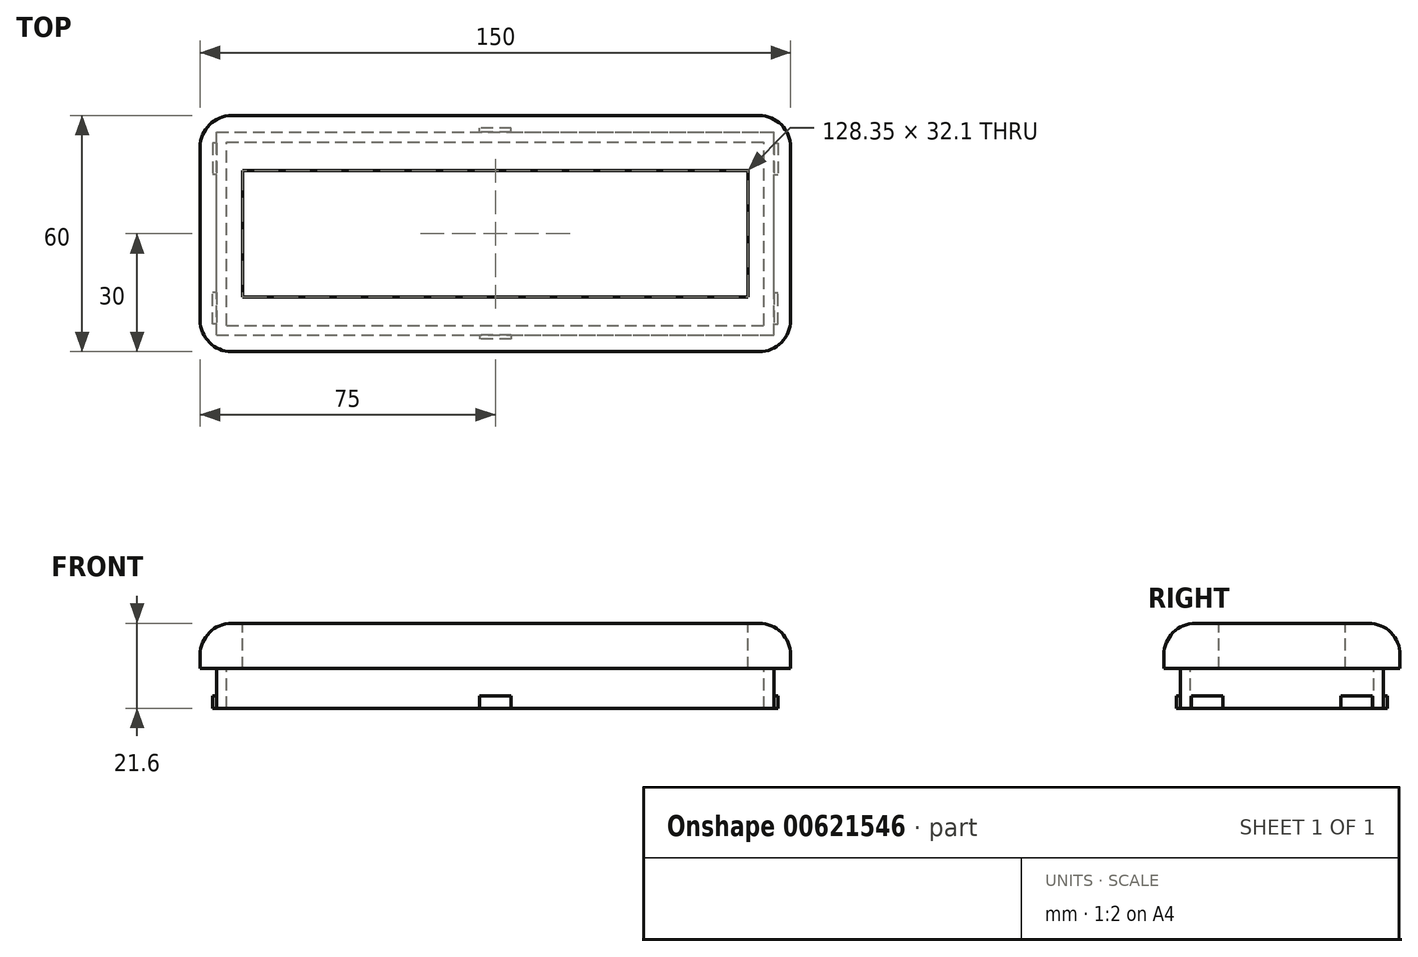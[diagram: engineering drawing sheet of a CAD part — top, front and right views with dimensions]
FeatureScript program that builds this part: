
annotation { "Feature Type Name" : "Feature", "Feature Type Description" : "" }
export const myFeature = defineFeature(function(context is Context, id is Id, definition is map)
    precondition{}
    {
        {
            var Q0;
            Q0=qCreatedBy(makeId("Top.planeOp"),FACE);
            var sketch = newSketch(context, id + "F0", { "sketchPlane" : qUnion([Q0])});
            skLineSegment(sketch, "E0.bottom", {"start": v(75, -30) * mm, "end": v(-75, -30) * mm});
            skLineSegment(sketch, "E0.top", {"start": v(75, 30) * mm, "end": v(-75, 30) * mm});
            skLineSegment(sketch, "E0.left", {"start": v(75, -30) * mm, "end": v(75, 30) * mm});
            skLineSegment(sketch, "E0.right", {"start": v(-75, -30) * mm, "end": v(-75, 30) * mm});
            skPoint(sketch, "E0.middle", {"position": v(0, 0) * mm});
            skSolve(sketch);
        }
        {
            var Q0;
            Q0 = qSketchRegion(id + "F0", true);
            extrude(context, id + "F1", {"entities" : qUnion([Q0]), "depth" : 11.5 * mm, "offsetDistance" : 25 * mm});
        }
        {
            var Q0;
            Q0=makeQuery(id+"F1.opExtrude","CAP_FACE",FACE,{"disambiguationData":[OSD([sQuery(id+"F0.wireOp",EDGE,"E0.bottom"),sQuery(id+"F0.wireOp",EDGE,"E0.top"),sQuery(id+"F0.wireOp",EDGE,"E0.left"),sQuery(id+"F0.wireOp",EDGE,"E0.right")])],"isStart":false});
            var sketch = newSketch(context, id + "F2", { "sketchPlane" : qUnion([Q0])});
            skLineSegment(sketch, "E1.bottom", {"start": v(64.17, 16.05) * mm, "end": v(-64.17, 16.05) * mm});
            skLineSegment(sketch, "E1.top", {"start": v(64.17, -16.05) * mm, "end": v(-64.17, -16.05) * mm});
            skLineSegment(sketch, "E1.left", {"start": v(64.17, 16.05) * mm, "end": v(64.17, -16.05) * mm});
            skLineSegment(sketch, "E1.right", {"start": v(-64.17, 16.05) * mm, "end": v(-64.17, -16.05) * mm});
            skPoint(sketch, "E1.middle", {"position": v(0, 0) * mm});
            skSolve(sketch);
        }
        {
            var Q0;
            Q0=makeQuery(id+"F2.imprint","IMPRINT",FACE,{"disambiguationData":[TD([[makeQuery(id+"F2.imprint","IMPRINT",EDGE,{"derivedFrom":sQuery(id+"F2.wireOp",EDGE,"E1.bottom")}),1.0]])]});
            extrude(context, id + "F3", {"entities" : qUnion([Q0]), "operationType" : NewBodyOperationType.REMOVE, "endBound" : BoundingType.UP_TO_NEXT, "oppositeDirection" : true, "depth" : 25 * mm, "offsetDistance" : 25 * mm});
        }
        {
            var Q0;
            Q0=makeQuery(id+"F1.opExtrude","SWEPT_EDGE",EDGE,{"disambiguationData":[OSD([sQuery(id+"F0.wireOp",EDGE,"E0.top"),sQuery(id+"F0.wireOp",EDGE,"E0.right")])]});
            var Q1;
            Q1=makeQuery(id+"F1.opExtrude","SWEPT_EDGE",EDGE,{"disambiguationData":[OSD([sQuery(id+"F0.wireOp",EDGE,"E0.top"),sQuery(id+"F0.wireOp",EDGE,"E0.left")])]});
            var Q2;
            Q2=makeQuery(id+"F1.opExtrude","SWEPT_EDGE",EDGE,{"disambiguationData":[OSD([sQuery(id+"F0.wireOp",EDGE,"E0.bottom"),sQuery(id+"F0.wireOp",EDGE,"E0.left")])]});
            var Q3;
            Q3=makeQuery(id+"F1.opExtrude","SWEPT_EDGE",EDGE,{"disambiguationData":[OSD([sQuery(id+"F0.wireOp",EDGE,"E0.bottom"),sQuery(id+"F0.wireOp",EDGE,"E0.right")])]});
            fillet(context, id + "F4", {"entities" : qUnion([Q0, Q1, Q2, Q3]), "radius" : 8 * mm, "tangentPropagation" : true, "allowEdgeOverflow" : false});
        }
        {
            var Q0;
            Q0=makeQuery(id+"F1.opExtrude","CAP_FACE",FACE,{"disambiguationData":[OSD([sQuery(id+"F0.wireOp",EDGE,"E0.bottom"),sQuery(id+"F0.wireOp",EDGE,"E0.top"),sQuery(id+"F0.wireOp",EDGE,"E0.left"),sQuery(id+"F0.wireOp",EDGE,"E0.right")])],"isStart":true});
            var sketch = newSketch(context, id + "F5", { "sketchPlane" : qUnion([Q0])});
            skLineSegment(sketch, "E2.bottom", {"start": v(-70.8, 25.8) * mm, "end": v(70.8, 25.8) * mm});
            skLineSegment(sketch, "E2.top", {"start": v(-70.8, -25.8) * mm, "end": v(70.8, -25.8) * mm});
            skLineSegment(sketch, "E2.left", {"start": v(-70.8, 25.8) * mm, "end": v(-70.8, -25.8) * mm});
            skLineSegment(sketch, "E2.right", {"start": v(70.8, 25.8) * mm, "end": v(70.8, -25.8) * mm});
            skLineSegment(sketch, "E3.0", {"start": v(-68.3, 23.3) * mm, "end": v(68.3, 23.3) * mm});
            skLineSegment(sketch, "E3.1", {"start": v(-68.3, 23.3) * mm, "end": v(-68.3, -23.3) * mm});
            skLineSegment(sketch, "E3.2", {"start": v(-68.3, -23.3) * mm, "end": v(68.3, -23.3) * mm});
            skLineSegment(sketch, "E3.3", {"start": v(68.3, 23.3) * mm, "end": v(68.3, -23.3) * mm});
            skSolve(sketch);
        }
        {
            var Q0;
            Q0=makeQuery(id+"F5.imprint","IMPRINT",FACE,{"disambiguationData":[TD([[makeQuery(id+"F5.imprint","IMPRINT",EDGE,{"derivedFrom":sQuery(id+"F5.wireOp",EDGE,"E2.bottom")}),-1.0]])]});
            extrude(context, id + "F6", {"entities" : qUnion([Q0]), "operationType" : NewBodyOperationType.ADD, "depth" : 10.1 * mm, "offsetDistance" : 25 * mm});
        }
        {
            var Q0;
            Q0=makeQuery(id+"F1.opExtrude","CAP_EDGE",EDGE,{"disambiguationData":[OSD([sQuery(id+"F0.wireOp",EDGE,"E0.top")])],"isStart":false});
            fillet(context, id + "F7", {"entities" : qUnion([Q0]), "radius" : 8 * mm, "tangentPropagation" : true, "allowEdgeOverflow" : false});
        }
        {
            var Q0;
            Q0=makeQuery(id+"F6.opExtrude","CAP_FACE",FACE,{"disambiguationData":[OSD([sQuery(id+"F5.wireOp",EDGE,"E2.bottom"),sQuery(id+"F5.wireOp",EDGE,"E2.top"),sQuery(id+"F5.wireOp",EDGE,"E2.left"),sQuery(id+"F5.wireOp",EDGE,"E2.right"),sQuery(id+"F5.wireOp",EDGE,"E3.0"),sQuery(id+"F5.wireOp",EDGE,"E3.1"),sQuery(id+"F5.wireOp",EDGE,"E3.2"),sQuery(id+"F5.wireOp",EDGE,"E3.3")])],"isStart":false});
            var sketch = newSketch(context, id + "F8", { "sketchPlane" : qUnion([Q0])});
            skLineSegment(sketch, "E4.bottom", {"start": v(-70.8, 22.98) * mm, "end": v(-71.8, 22.98) * mm});
            skLineSegment(sketch, "E4.top", {"start": v(-70.8, 14.98) * mm, "end": v(-71.8, 14.98) * mm});
            skLineSegment(sketch, "E4.left", {"start": v(-70.8, 22.98) * mm, "end": v(-70.8, 14.98) * mm});
            skLineSegment(sketch, "E4.right", {"start": v(-71.8, 22.98) * mm, "end": v(-71.8, 14.98) * mm});
            skLineSegment(sketch, "E5.MirrorCS", {"start": v(70.8, 22.98) * mm, "end": v(71.8, 22.98) * mm});
            skLineSegment(sketch, "E6.MirrorCS", {"start": v(70.8, 14.98) * mm, "end": v(71.8, 14.98) * mm});
            skLineSegment(sketch, "E7.MirrorCS", {"start": v(70.8, 22.98) * mm, "end": v(70.8, 14.98) * mm});
            skLineSegment(sketch, "E8.MirrorCS", {"start": v(71.8, 22.98) * mm, "end": v(71.8, 14.98) * mm});
            skLineSegment(sketch, "E9.MirrorCS", {"start": v(-71.8, -22.98) * mm, "end": v(-71.8, -14.98) * mm});
            skLineSegment(sketch, "E10.MirrorCS", {"start": v(-70.8, -22.98) * mm, "end": v(-70.8, -14.98) * mm});
            skLineSegment(sketch, "E11.MirrorCS", {"start": v(-70.8, -14.98) * mm, "end": v(-71.8, -14.98) * mm});
            skLineSegment(sketch, "E12.MirrorCS", {"start": v(-70.8, -22.98) * mm, "end": v(-71.8, -22.98) * mm});
            skLineSegment(sketch, "E13.MirrorCS", {"start": v(71.8, -22.98) * mm, "end": v(71.8, -14.98) * mm});
            skLineSegment(sketch, "E14.MirrorCS", {"start": v(70.8, -14.98) * mm, "end": v(71.8, -14.98) * mm});
            skLineSegment(sketch, "E15.MirrorCS", {"start": v(70.8, -22.98) * mm, "end": v(70.8, -14.98) * mm});
            skLineSegment(sketch, "E16.MirrorCS", {"start": v(70.8, -22.98) * mm, "end": v(71.8, -22.98) * mm});
            skLineSegment(sketch, "E17.bottom", {"start": v(4, 25.8) * mm, "end": v(0, 25.8) * mm});
            skLineSegment(sketch, "E17.top", {"start": v(4, 26.8) * mm, "end": v(0, 26.8) * mm});
            skLineSegment(sketch, "E17.left", {"start": v(4, 25.8) * mm, "end": v(4, 26.8) * mm});
            skLineSegment(sketch, "E17.right", {"start": v(0, 25.8) * mm, "end": v(0, 26.8) * mm});
            skLineSegment(sketch, "E18.MirrorCS", {"start": v(-4, 25.8) * mm, "end": v(-4, 26.8) * mm});
            skLineSegment(sketch, "E19.MirrorCS", {"start": v(-4, 26.8) * mm, "end": v(0, 26.8) * mm});
            skLineSegment(sketch, "E20.MirrorCS", {"start": v(-4, 25.8) * mm, "end": v(0, 25.8) * mm});
            skLineSegment(sketch, "E21.MirrorCS", {"start": v(0, -25.8) * mm, "end": v(0, -26.8) * mm});
            skLineSegment(sketch, "E22.MirrorCS", {"start": v(4, -25.8) * mm, "end": v(0, -25.8) * mm});
            skLineSegment(sketch, "E23.MirrorCS", {"start": v(-4, -26.8) * mm, "end": v(0, -26.8) * mm});
            skLineSegment(sketch, "E24.MirrorCS", {"start": v(-4, -25.8) * mm, "end": v(-4, -26.8) * mm});
            skLineSegment(sketch, "E25.MirrorCS", {"start": v(-4, -25.8) * mm, "end": v(0, -25.8) * mm});
            skLineSegment(sketch, "E26.MirrorCS", {"start": v(4, -26.8) * mm, "end": v(0, -26.8) * mm});
            skLineSegment(sketch, "E27.MirrorCS", {"start": v(4, -25.8) * mm, "end": v(4, -26.8) * mm});
            skSolve(sketch);
        }
        {
            var Q0;
            {var subQ0=sQuery(id+"F0.wireOp",EDGE,"E0.right");var subQ1=sQuery(id+"F0.wireOp",EDGE,"E0.top");var subQ2=sQuery(id+"F0.wireOp",EDGE,"E0.bottom");var subQ3=sQuery(id+"F0.wireOp",EDGE,"E0.left");Q0=makeQuery(id+"F6.boolean.opBoolean","SPLIT",FACE,{"disambiguationData":[TD([makeQuery(id+"F1.opExtrude","SWEPT_FACE",FACE,{"disambiguationData":[OSD([subQ2])]})])],"derivedFrom":makeQuery(id+"F1.opExtrude","CAP_FACE",FACE,{"disambiguationData":[OSD([subQ2,subQ1,subQ3,subQ0])],"isStart":true})});}
            cPlane(context, id + "F9", {"entities" : qUnion([Q0]), "cplaneType" : CPlaneType.OFFSET, "offset" : 7 * mm, "width" : 150 * mm, "height" : 150 * mm});
        }
        {
            var Q0;
            Q0 = qSketchRegion(id + "F8", true);
            var Q1;
            Q1=qCreatedBy(id+"F9.planeOp",FACE);
            extrude(context, id + "F10", {"entities" : qUnion([Q0]), "operationType" : NewBodyOperationType.ADD, "endBound" : BoundingType.UP_TO_SURFACE, "oppositeDirection" : true, "depth" : 2 * mm, "endBoundEntityFace" : qUnion([Q1]), "offsetDistance" : 25 * mm});
        }
    });
